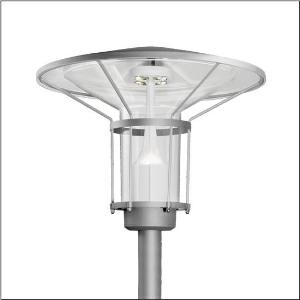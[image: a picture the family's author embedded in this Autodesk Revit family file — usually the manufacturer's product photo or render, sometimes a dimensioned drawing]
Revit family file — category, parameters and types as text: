
# Revit family: laterne_classic_iq___st1_2a_5xa5245mf14hp_5b72
name_source: partatom
category: Lighting Fixtures
units: mm (PartAtom-declared; Revit-internal decimal feet)

## family parameters
Cut with Voids When Loaded = No
Host = Face
Light Source = No
Part Type = Normal
Room Calculation Point = No
Round Connector Dimension = Use Diameter
Shared = No

## types (1)
- --- (1 x LED, 3800 lm, 33.6 W, 2700K)
    Apparent Load = 34 VA
    CIE Flux Codes = 22 60 93 98 100
    Color Rendering = 70
    Color Temperature = 2700K
    Default Elevation = 1800 mm
    Description = Lantern Classic iQ, mast luminaire, Module 540 iQ-SR, primary light control with 3 zone facetted reflector, of plastic, silver coated, highly specular, structured, primary optical cover: cover, of PMMA, transparent, light distribution: ST1.2a, light emission: direct distribution, primary light characteristic: asymmetric, installation type: post-top, LED, High Power LED, rated luminous flux: 3.800lm, luminous efficacy: 113lm/W, light colour: 727, colour temperature: 2700K, control gear: ECG iQ, control: presetting dimming logarithmic, Street-Remote, Auto-Match, Temp-Guard, Lumen-Switch, Night-Set, Smart-Wire, Light-Fading, Desk-Remote (wireless, voltage-free reading and setting of iQ features in the workshop via application-optimized NFC function/RFID function), optimised constant luminous flux control (CLO 2.0), with terminal, 6-pole, max. 2.5mm², mains connection: 230..240V, AC, 50/60Hz, start of lifetime: 34W, end of service life: 36W, reduction: 15W, luminaire housing, upper part, of glass-fibre reinforced polyester, coated, Siteco® metallic grey (DB 702S), diameter: 750mm, height: 596mm, spigot size: d x l = 76 x 70mm (post-top) | with reducer (optional accessory) 60 x 70mm, post-top mast mounting element, of diecast aluminium, coated, Siteco® metallic grey (DB 702S), Module 540 iQ-SR, traffic white (RAL 9016), equipment: Power, protection rating (complete): IP65, insulation class (complete): insulation class II (safety insulation), certification: CE, ENEC, VDE, packaging unit: 1 piece

Light Distribution: ST1.2a
    Height = 596 mm
    Lamp = 1 x LED
    Lamp Light Flux = 3800 lm
    Lamp Power = 33.6 W
    Lamp count = 1
    Length = 750 mm
    Luminous efficacy = 113 lm/W
    Manufacturer = Siteco
    ModVariant = No
    Model = 5XA5245MF14HP
    Number of Poles = 1
    OnlyDefault = Yes
    Power Factor = 1
    Product Name = Laterne Classic iQ | ST1.2a
    Product group = mast luminaire | pylon top
    ProductGroupID = 6100
    Protection Class = Protection class II
    Protection Degree = IP 65
    RLX_Detail_Level = 1
    RLX_Emergency_Light_Flux = 0 lm
    RLX_Emergency_Type = 0
    RLX_Emergency_Type_DB = No
    RlxData = <blob elided: 64825 chars, md5=feb6c10b>
    Socket = socket
    Standby Power = 0 W
    System Light Flux = 3800 lm
    System Power = 34 W
    Type Comments = factory setting: luminous flux: 100 % | dim-lin: 254 | 695 mA
    Type Image = l_1006052.jpg
    URL = http://relux.com
    VarID = @adj_102811
    Voltage = 0 V
    Weight = 0.00 kg
    Width = 0 mm  [stored 0 ft]

note: [stored X ft] marks values corroborated as IEEE doubles in the binary element streams (Revit-internal decimal feet)

## geometry (parser evidence)
native form markers: Blend x4, Sweep x9
no freeform markers — native parametric forms only
